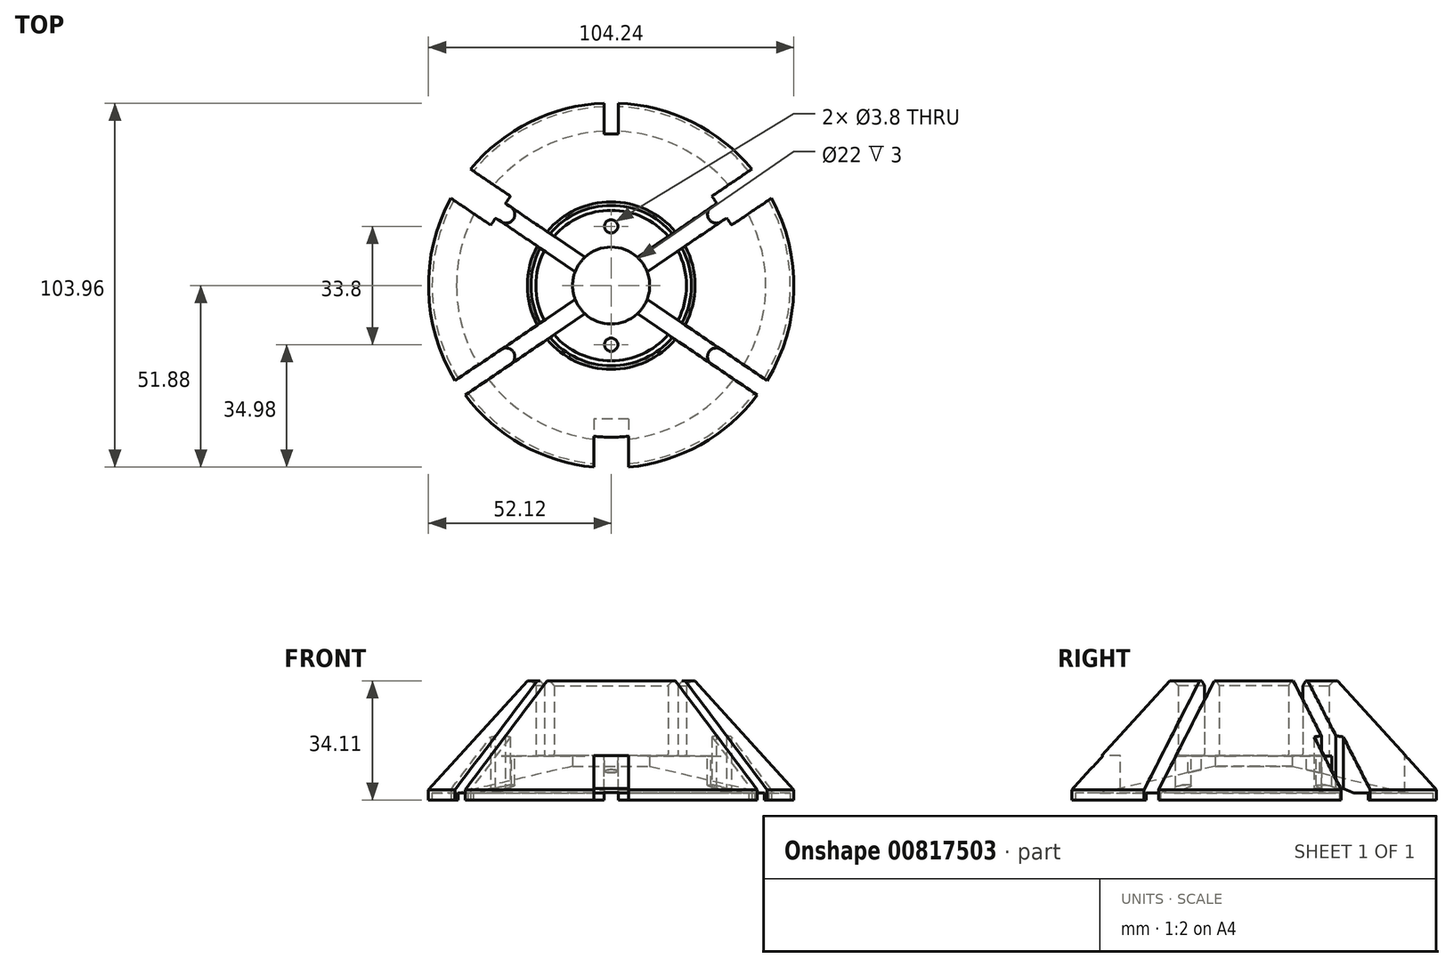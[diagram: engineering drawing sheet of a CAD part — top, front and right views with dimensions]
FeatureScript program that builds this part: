
annotation { "Feature Type Name" : "Feature", "Feature Type Description" : "" }
export const myFeature = defineFeature(function(context is Context, id is Id, definition is map)
    precondition{}
    {
        {
            var Q0;
            Q0=qCreatedBy(makeId("Right.planeOp"),FACE);
            var sketch = newSketch(context, id + "F0", { "sketchPlane" : qUnion([Q0])});
            skLineSegment(sketch, "E0", {"start": v(0, 0) * mm, "end": v(-11, 0) * mm});
            skLineSegment(sketch, "E1", {"start": v(-11, 3) * mm, "end": v(-21.5, 3) * mm});
            skLineSegment(sketch, "E2", {"start": v(-21.5, 3) * mm, "end": v(-21.5, 23) * mm});
            skLineSegment(sketch, "E3", {"start": v(-21.5, 23) * mm, "end": v(-22.9, 24.42) * mm});
            skLineSegment(sketch, "E4", {"start": v(-22.9, 24.42) * mm, "end": v(-23.9, 24.42) * mm});
            skLineSegment(sketch, "E5", {"start": v(-23.9, 24.42) * mm, "end": v(-52.12, -6.69) * mm});
            skLineSegment(sketch, "E6", {"start": v(-52.12, -6.69) * mm, "end": v(-52.12, -9.69) * mm});
            skLineSegment(sketch, "E7", {"start": v(-52.12, -9.69) * mm, "end": v(-51.12, -9.69) * mm});
            skLineSegment(sketch, "E8", {"start": v(-51.12, -9.69) * mm, "end": v(-51.12, -7.69) * mm});
            skLineSegment(sketch, "E9", {"start": v(-51.12, -7.69) * mm, "end": v(-44.12, -7.69) * mm});
            skLineSegment(sketch, "E10", {"start": v(-44.12, -7.69) * mm, "end": v(-11, 0) * mm});
            skLineSegment(sketch, "E11", {"start": v(-11, 3) * mm, "end": v(0, 3) * mm});
            skLineSegment(sketch, "E12", {"start": v(0, -21) * mm, "end": v(0, 31.87) * mm});
            skSolve(sketch);
        }
        {
            var Q0;
            {var subQ0=sQuery(id+"F0.wireOp",EDGE,"E0");Q0=makeQuery(id+"F0.imprint","IMPRINT",FACE,{"disambiguationData":[TD([[makeQuery(id+"F0.imprint","IMPRINT",EDGE,{"derivedFrom":subQ0}),-1.0]])]});}
            var Q1;
            Q1=sQuery(id+"F0.wireOp",EDGE,"E12");
            revolve(context, id + "F1", {"surfaceOperationType" : NewSurfaceOperationType.NEW, "entities" : qUnion([Q0]), "axis" : qUnion([Q1]), "revolveType" : RevolveType.FULL});
        }
        {
            var Q0;
            Q0=makeQuery(id+"F1.opRevolve","SWEPT_FACE",FACE,{"disambiguationData":[OSD([sQuery(id+"F0.wireOp",EDGE,"E0")])]});
            var sketch = newSketch(context, id + "F2", { "sketchPlane" : qUnion([Q0])});
            skCircle(sketch, "E13", {"center": v(0, 0) * mm, "radius": 11 * mm});
            skCircle(sketch, "E14", {"center": v(0, 0) * mm, "radius": 12 * mm});
            skSolve(sketch);
        }
        {
            var Q0;
            Q0=makeQuery(id+"F1.opRevolve","SWEPT_EDGE",EDGE,{"disambiguationData":[OSD([sQuery(id+"F0.wireOp",EDGE,"E1"),sQuery(id+"F0.wireOp",EDGE,"E2")])]});
            fillet(context, id + "F3", {"entities" : qUnion([Q0]), "radius" : .5 * mm, "tangentPropagation" : true, "allowEdgeOverflow" : false});
        }
        {
            var Q0;
            Q0=makeQuery(id+"F2.imprint","IMPRINT",FACE,{"disambiguationData":[TD([[makeQuery(id+"F2.imprint","IMPRINT",EDGE,{"derivedFrom":sQuery(id+"F2.wireOp",EDGE,"E13")}),1.0]])]});
            extrude(context, id + "F4", {"entities" : qUnion([Q0]), "operationType" : NewBodyOperationType.REMOVE, "oppositeDirection" : true, "depth" : 25 * mm, "offsetDistance" : 25 * mm});
        }
        {
            var Q0;
            Q0=makeQuery(id+"F1.opRevolve","SWEPT_FACE",FACE,{"disambiguationData":[OSD([sQuery(id+"F0.wireOp",EDGE,"E1"),sQuery(id+"F0.wireOp",EDGE,"E11")])]});
            var sketch = newSketch(context, id + "F5", { "sketchPlane" : qUnion([Q0])});
            skCircle(sketch, "E15", {"center": v(0, 16.9) * mm, "radius": 1.9 * mm});
            skCircle(sketch, "E16", {"center": v(0, -16.9) * mm, "radius": 1.9 * mm});
            skSolve(sketch);
        }
        {
            var Q0;
            Q0 = qSketchRegion(id + "F5", true);
            extrude(context, id + "F6", {"entities" : qUnion([Q0]), "operationType" : NewBodyOperationType.REMOVE, "oppositeDirection" : true, "depth" : 25 * mm, "offsetDistance" : 25 * mm});
        }
        {
            var Q0;
            Q0=makeQuery(id+"F1.opRevolve","SWEPT_FACE",FACE,{"disambiguationData":[OSD([sQuery(id+"F0.wireOp",EDGE,"E1"),sQuery(id+"F0.wireOp",EDGE,"E11")])]});
            var sketch = newSketch(context, id + "F7", { "sketchPlane" : qUnion([Q0])});
            skLineSegment(sketch, "E17.bottom", {"start": v(5, -38.12) * mm, "end": v(-5, -38.12) * mm});
            skLineSegment(sketch, "E17.top", {"start": v(5, -66.12) * mm, "end": v(-5, -66.12) * mm});
            skLineSegment(sketch, "E17.left", {"start": v(5, -38.12) * mm, "end": v(5, -66.12) * mm});
            skLineSegment(sketch, "E17.right", {"start": v(-5, -38.12) * mm, "end": v(-5, -66.12) * mm});
            skPoint(sketch, "E17.middle", {"position": v(0, -52.12) * mm});
            skLineSegment(sketch, "E18.bottom", {"start": v(2, 43.12) * mm, "end": v(-2, 43.12) * mm});
            skLineSegment(sketch, "E18.top", {"start": v(2, 61.12) * mm, "end": v(-2, 61.12) * mm});
            skLineSegment(sketch, "E18.left", {"start": v(2, 43.12) * mm, "end": v(2, 61.12) * mm});
            skLineSegment(sketch, "E18.right", {"start": v(-2, 43.12) * mm, "end": v(-2, 61.12) * mm});
            skPoint(sketch, "E18.middle", {"position": v(0, 52.12) * mm});
            skSolve(sketch);
        }
        {
            var Q0;
            Q0 = qSketchRegion(id + "F7", true);
            extrude(context, id + "F8", {"entities" : qUnion([Q0]), "operationType" : NewBodyOperationType.REMOVE, "endBound" : BoundingType.THROUGH_ALL, "oppositeDirection" : true, "depth" : 25 * mm, "offsetDistance" : 25 * mm});
        }
        {
            var Q0;
            Q0=makeQuery(id+"F1.opRevolve","SWEPT_FACE",FACE,{"disambiguationData":[OSD([sQuery(id+"F0.wireOp",EDGE,"E4")])]});
            var sketch = newSketch(context, id + "F9", { "sketchPlane" : qUnion([Q0])});
            skLineSegment(sketch, "E19", {"start": v(-60.69, 44.14) * mm, "end": v(63.5, -40) * mm});
            skLineSegment(sketch, "E20", {"start": v(63.5, -40) * mm, "end": v(60.69, -44.14) * mm});
            skLineSegment(sketch, "E21", {"start": v(60.69, -44.14) * mm, "end": v(-63.5, 40) * mm});
            skLineSegment(sketch, "E22", {"start": v(-63.5, 40) * mm, "end": v(-60.69, 44.14) * mm});
            skLineSegment(sketch, "E23.MirrorCS", {"start": v(-60.69, -44.14) * mm, "end": v(63.5, 40) * mm});
            skLineSegment(sketch, "E24.MirrorCS", {"start": v(-63.5, -40) * mm, "end": v(-60.69, -44.14) * mm});
            skLineSegment(sketch, "E25.MirrorCS", {"start": v(60.69, 44.14) * mm, "end": v(-63.5, -40) * mm});
            skLineSegment(sketch, "E26.MirrorCS", {"start": v(63.5, 40) * mm, "end": v(60.69, 44.14) * mm});
            skSolve(sketch);
        }
        {
            var Q0;
            Q0 = qSketchRegion(id + "F9", true);
            extrude(context, id + "F10", {"entities" : qUnion([Q0]), "operationType" : NewBodyOperationType.REMOVE, "oppositeDirection" : true, "depth" : 21.5 * mm, "offsetDistance" : 25 * mm});
        }
        {
            var Q0;
            {var subQ0=sQuery(id+"F0.wireOp",EDGE,"E5");var subQ1=sQuery(id+"F9.wireOp",EDGE,"E25.MirrorCS");var subQ2=sQuery(id+"F9.wireOp",EDGE,"E19");var subQ3=sQuery(id+"F0.wireOp",EDGE,"E4");var subQ6=makeQuery(id+"F1.opRevolve","SWEPT_EDGE",EDGE,{"disambiguationData":[OSD([subQ3,subQ0])]});var subQ7=makeQuery(id+"F9.imprint","INTERSECT",VERTEX,{"disambiguationData":[OD(0.0)],"derivedFrom":[subQ6,subQ2]});var subQ8=sQuery(id+"F9.wireOp",EDGE,"E22");var subQ9=sQuery(id+"F9.wireOp",EDGE,"E21");Q0=makeQuery(id+"F10.boolean.opBoolean","COPY",FACE,{"disambiguationData":[TD([makeQuery(id+"F10.opExtrude","SWEPT_FACE",FACE,{"disambiguationData":[OSD([subQ2]),TDD([makeQuery(id+"F9.imprint","IMPRINT",EDGE,{"disambiguationData":[TD([[makeQuery(id+"F9.imprint","INTERSECT",VERTEX,{"derivedFrom":[subQ2,subQ8]}),-1.0]])],"derivedFrom":subQ2}),makeQuery(id+"F9.imprint","IMPRINT",EDGE,{"disambiguationData":[TD([[subQ7,-1.0]])],"derivedFrom":subQ2}),makeQuery(id+"F9.imprint","IMPRINT",EDGE,{"disambiguationData":[TD([[makeQuery(id+"F9.imprint","INTERSECT",VERTEX,{"derivedFrom":[subQ2,subQ1]}),1.0]])],"derivedFrom":subQ2})])]})])],"derivedFrom":makeQuery(id+"F10.opExtrude","CAP_FACE",FACE,{"disambiguationData":[OSD([subQ2,sQuery(id+"F9.wireOp",EDGE,"E20"),subQ9,subQ8,sQuery(id+"F9.wireOp",EDGE,"E23.MirrorCS"),sQuery(id+"F9.wireOp",EDGE,"E24.MirrorCS"),subQ1,sQuery(id+"F9.wireOp",EDGE,"E26.MirrorCS")])],"isStart":false})});}
            var sketch = newSketch(context, id + "F11", { "sketchPlane" : qUnion([Q0])});
            skLineSegment(sketch, "E27", {"start": v(-30.16, 23.45) * mm, "end": v(-28.75, 25.52) * mm});
            skLineSegment(sketch, "E28", {"start": v(-28.75, 25.52) * mm, "end": v(-43.19, 35.3) * mm});
            skLineSegment(sketch, "E29", {"start": v(-43.19, 35.3) * mm, "end": v(-48.8, 27.02) * mm});
            skLineSegment(sketch, "E30", {"start": v(-48.8, 27.02) * mm, "end": v(-34.36, 17.24) * mm});
            skLineSegment(sketch, "E31", {"start": v(-34.36, 17.24) * mm, "end": v(-32.96, 19.31) * mm});
            skLineSegment(sketch, "E32.MirrorCS", {"start": v(43.19, 35.3) * mm, "end": v(48.8, 27.02) * mm});
            skLineSegment(sketch, "E33.MirrorCS", {"start": v(28.75, 25.52) * mm, "end": v(43.19, 35.3) * mm});
            skLineSegment(sketch, "E34.MirrorCS", {"start": v(30.16, 23.45) * mm, "end": v(28.75, 25.52) * mm});
            skLineSegment(sketch, "E35.MirrorCS", {"start": v(34.36, 17.24) * mm, "end": v(32.96, 19.31) * mm});
            skLineSegment(sketch, "E36.MirrorCS", {"start": v(48.8, 27.02) * mm, "end": v(34.36, 17.24) * mm});
            skLineSegment(sketch, "E37", {"start": v(-30.16, 23.45) * mm, "end": v(-32.96, 19.31) * mm});
            skLineSegment(sketch, "E38", {"start": v(-34.36, 17.24) * mm, "end": v(-28.75, 25.52) * mm});
            skLineSegment(sketch, "E39", {"start": v(28.75, 25.52) * mm, "end": v(34.36, 17.24) * mm});
            skSolve(sketch);
        }
        {
            var Q0;
            Q0=makeQuery(id+"F11.imprint","IMPRINT",FACE,{"disambiguationData":[TD([[makeQuery(id+"F11.imprint","IMPRINT",EDGE,{"derivedFrom":sQuery(id+"F11.wireOp",EDGE,"E32.MirrorCS")}),-1.0]])]});
            var Q1;
            {var subQ15=sQuery(id+"F11.wireOp",EDGE,"E28");Q1=makeQuery(id+"F11.imprint","IMPRINT",FACE,{"disambiguationData":[TD([[makeQuery(id+"F11.imprint","IMPRINT",EDGE,{"derivedFrom":subQ15}),1.0]])]});}
            var Q2;
            {var subQ1=sQuery(id+"F9.wireOp",EDGE,"E22");var subQ2=sQuery(id+"F9.wireOp",EDGE,"E21");var subQ3=sQuery(id+"F0.wireOp",EDGE,"E5");var subQ9=sQuery(id+"F9.wireOp",EDGE,"E25.MirrorCS");var subQ12=sQuery(id+"F9.wireOp",EDGE,"E19");var subQ17=makeQuery(id+"F10.boolean.opBoolean","INTERSECT",EDGE,{"disambiguationData":[OD(0.0)],"derivedFrom":[makeQuery(id+"F1.opRevolve","SWEPT_FACE",FACE,{"disambiguationData":[OSD([subQ3])]}),makeQuery(id+"F10.opExtrude","CAP_FACE",FACE,{"disambiguationData":[OSD([subQ12,sQuery(id+"F9.wireOp",EDGE,"E20"),subQ2,subQ1,sQuery(id+"F9.wireOp",EDGE,"E23.MirrorCS"),sQuery(id+"F9.wireOp",EDGE,"E24.MirrorCS"),subQ9,sQuery(id+"F9.wireOp",EDGE,"E26.MirrorCS")])],"isStart":false})]});Q2=makeQuery(id+"F11.imprint","IMPRINT",FACE,{"disambiguationData":[TD([[makeQuery(id+"F11.imprint","IMPRINT",EDGE,{"derivedFrom":subQ17}),1.0]])]});}
            extrude(context, id + "F12", {"entities" : qUnion([Q0, Q1, Q2]), "operationType" : NewBodyOperationType.REMOVE, "endBound" : BoundingType.SYMMETRIC, "depth" : 30 * mm, "offsetDistance" : 25 * mm});
        }
        {
            var Q0;
            {var subQ0=sQuery(id+"F0.wireOp",EDGE,"E5");var subQ1=sQuery(id+"F9.wireOp",EDGE,"E23.MirrorCS");var subQ2=sQuery(id+"F9.wireOp",EDGE,"E21");var subQ3=sQuery(id+"F0.wireOp",EDGE,"E4");var subQ6=makeQuery(id+"F1.opRevolve","SWEPT_EDGE",EDGE,{"disambiguationData":[OSD([subQ3,subQ0])]});var subQ7=makeQuery(id+"F9.imprint","INTERSECT",VERTEX,{"disambiguationData":[OD(0.0)],"derivedFrom":[subQ6,subQ1]});var subQ8=sQuery(id+"F9.wireOp",EDGE,"E24.MirrorCS");var subQ9=sQuery(id+"F9.wireOp",EDGE,"E25.MirrorCS");Q0=makeQuery(id+"F10.boolean.opBoolean","COPY",FACE,{"disambiguationData":[TD([makeQuery(id+"F10.opExtrude","SWEPT_FACE",FACE,{"disambiguationData":[OSD([subQ1]),TDD([makeQuery(id+"F9.imprint","IMPRINT",EDGE,{"disambiguationData":[TD([[makeQuery(id+"F9.imprint","INTERSECT",VERTEX,{"derivedFrom":[subQ1,subQ8]}),-1.0]])],"derivedFrom":subQ1}),makeQuery(id+"F9.imprint","IMPRINT",EDGE,{"disambiguationData":[TD([[subQ7,-1.0]])],"derivedFrom":subQ1}),makeQuery(id+"F9.imprint","IMPRINT",EDGE,{"disambiguationData":[TD([[makeQuery(id+"F9.imprint","INTERSECT",VERTEX,{"derivedFrom":[subQ2,subQ1]}),1.0]])],"derivedFrom":subQ1})])]})])],"derivedFrom":makeQuery(id+"F10.opExtrude","CAP_FACE",FACE,{"disambiguationData":[OSD([sQuery(id+"F9.wireOp",EDGE,"E19"),sQuery(id+"F9.wireOp",EDGE,"E20"),subQ2,sQuery(id+"F9.wireOp",EDGE,"E22"),subQ1,subQ8,subQ9,sQuery(id+"F9.wireOp",EDGE,"E26.MirrorCS")])],"isStart":false})});}
            var sketch = newSketch(context, id + "F13", { "sketchPlane" : qUnion([Q0])});
            skLineSegment(sketch, "E40", {"start": v(-31.4, -18.26) * mm, "end": v(-47.43, -29.12) * mm});
            skLineSegment(sketch, "E41", {"start": v(-47.43, -29.12) * mm, "end": v(-44.62, -33.25) * mm});
            skLineSegment(sketch, "E42", {"start": v(-44.62, -33.25) * mm, "end": v(-28.44, -22.3) * mm});
            skLineSegment(sketch, "E43", {"start": v(-28.44, -22.3) * mm, "end": v(-31.4, -18.26) * mm});
            skLineSegment(sketch, "E44.MirrorCS", {"start": v(47.43, -29.12) * mm, "end": v(44.62, -33.25) * mm});
            skLineSegment(sketch, "E45.MirrorCS", {"start": v(31.4, -18.26) * mm, "end": v(47.43, -29.12) * mm});
            skLineSegment(sketch, "E46.MirrorCS", {"start": v(28.44, -22.3) * mm, "end": v(31.4, -18.26) * mm});
            skLineSegment(sketch, "E47.MirrorCS", {"start": v(44.62, -33.25) * mm, "end": v(28.44, -22.3) * mm});
            skArc(sketch, "E48", {"start": v(-28.44, -22.3) * mm, "mid": v(-27.98, -18.85) * mm, "end": v(-31.4, -18.26) * mm});
            skArc(sketch, "E49.MirrorCS", {"start": v(28.44, -22.3) * mm, "mid": v(27.98, -18.85) * mm, "end": v(31.4, -18.26) * mm});
            skLineSegment(sketch, "E50.MirrorCS", {"start": v(-28.44, 22.3) * mm, "end": v(-31.4, 18.26) * mm});
            skLineSegment(sketch, "E51.MirrorCS", {"start": v(-47.43, 29.12) * mm, "end": v(-44.62, 33.25) * mm});
            skArc(sketch, "E52.MirrorCS", {"start": v(-28.44, 22.3) * mm, "mid": v(-27.98, 18.85) * mm, "end": v(-31.4, 18.26) * mm});
            skLineSegment(sketch, "E53.MirrorCS", {"start": v(-31.4, 18.26) * mm, "end": v(-47.43, 29.12) * mm});
            skLineSegment(sketch, "E54.MirrorCS", {"start": v(-44.62, 33.25) * mm, "end": v(-28.44, 22.3) * mm});
            skLineSegment(sketch, "E55.MirrorCS", {"start": v(28.44, 22.3) * mm, "end": v(31.4, 18.26) * mm});
            skLineSegment(sketch, "E56.MirrorCS", {"start": v(47.43, 29.12) * mm, "end": v(44.62, 33.25) * mm});
            skLineSegment(sketch, "E57.MirrorCS", {"start": v(31.4, 18.26) * mm, "end": v(47.43, 29.12) * mm});
            skLineSegment(sketch, "E58.MirrorCS", {"start": v(44.62, 33.25) * mm, "end": v(28.44, 22.3) * mm});
            skArc(sketch, "E59.MirrorCS", {"start": v(28.44, 22.3) * mm, "mid": v(27.98, 18.85) * mm, "end": v(31.4, 18.26) * mm});
            skSolve(sketch);
        }
        {
            var Q0;
            Q0 = qSketchRegion(id + "F13", true);
            extrude(context, id + "F14", {"entities" : qUnion([Q0]), "operationType" : NewBodyOperationType.REMOVE, "endBound" : BoundingType.SYMMETRIC, "oppositeDirection" : true, "depth" : 30 * mm, "offsetDistance" : 25 * mm});
        }
    });
